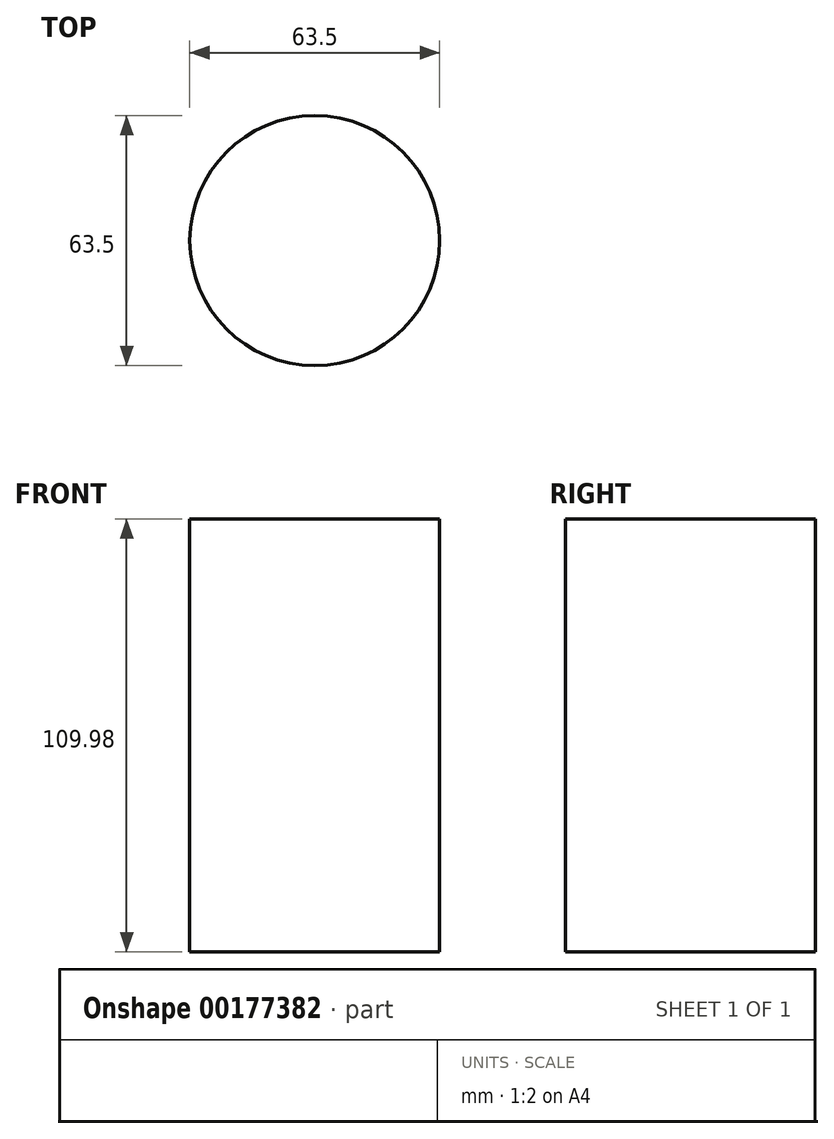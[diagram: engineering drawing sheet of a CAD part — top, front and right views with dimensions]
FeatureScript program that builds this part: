
annotation { "Feature Type Name" : "Feature", "Feature Type Description" : "" }
export const myFeature = defineFeature(function(context is Context, id is Id, definition is map)
    precondition{}
    {
        {
            var Q0;
            Q0=qCreatedBy(makeId("Top.planeOp"),FACE);
            var sketch = newSketch(context, id + "F0", { "sketchPlane" : qUnion([Q0])});
            skCircle(sketch, "E0", {"center": v(0, 0) * mm, "radius": 31.75 * mm});
            skSolve(sketch);
        }
        {
            var Q0;
            Q0=makeQuery(id+"F0.imprint","IMPRINT",FACE,{"disambiguationData":[TD([[makeQuery(id+"F0.imprint","IMPRINT",EDGE,{"derivedFrom":sQuery(id+"F0.wireOp",EDGE,"E0")}),1.0]])]});
            extrude(context, id + "F1", {"entities" : qUnion([Q0]), "depth" : 109.98 * mm});
        }
    });
